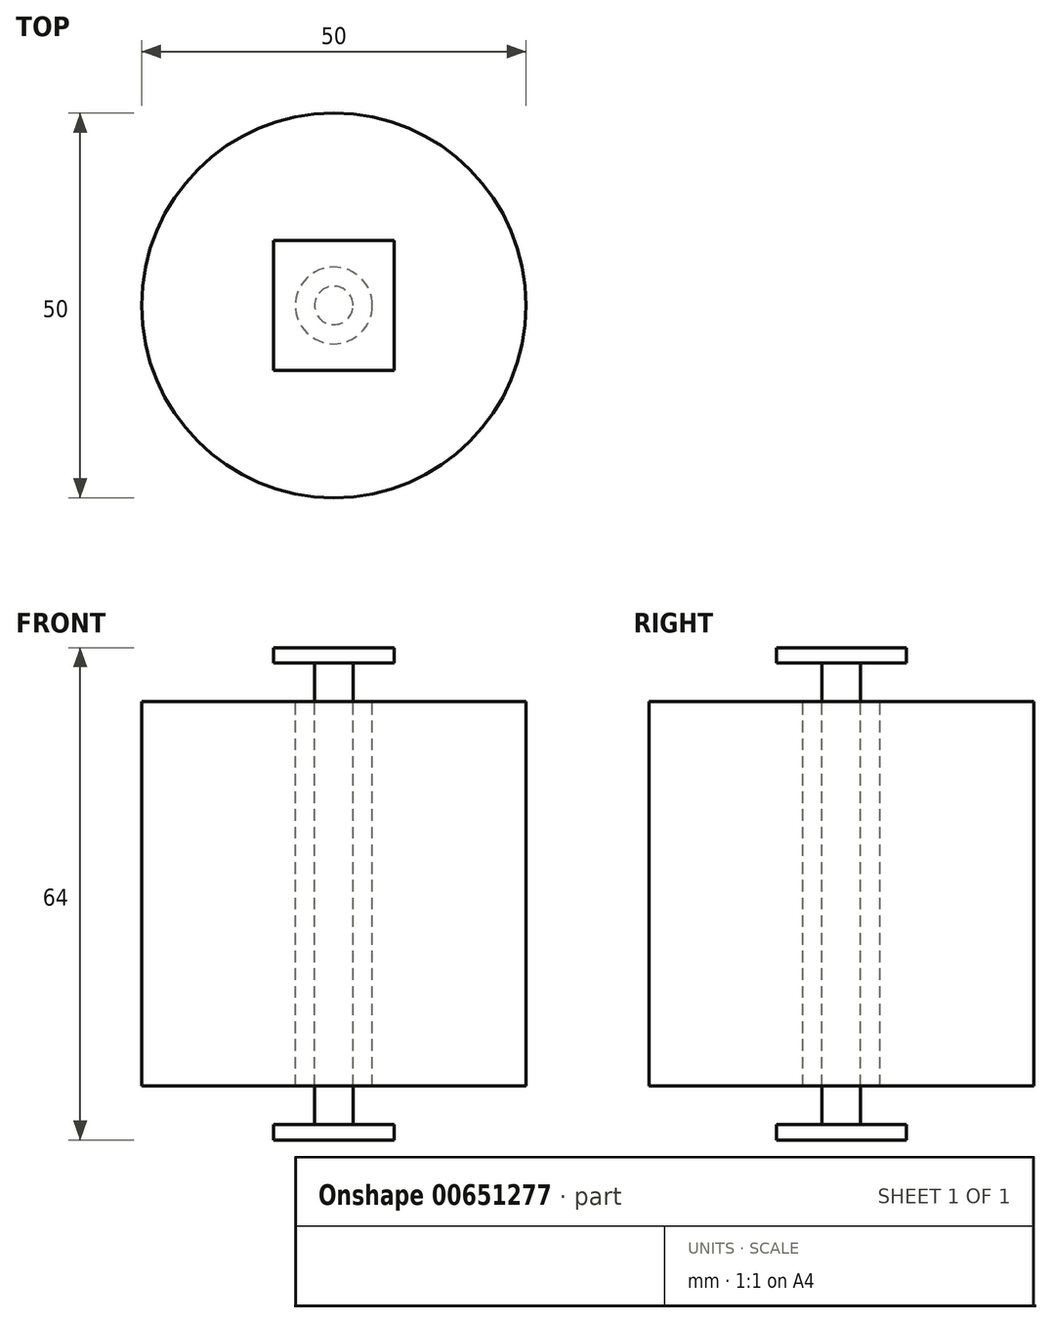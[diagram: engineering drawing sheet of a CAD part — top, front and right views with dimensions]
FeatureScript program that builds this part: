
annotation { "Feature Type Name" : "Feature", "Feature Type Description" : "" }
export const myFeature = defineFeature(function(context is Context, id is Id, definition is map)
    precondition{}
    {
        {
            var Q0;
            Q0=qCreatedBy(makeId("Top.planeOp"),FACE);
            var sketch = newSketch(context, id + "F0", { "sketchPlane" : qUnion([Q0])});
            skCircle(sketch, "E0", {"center": v(0, 0) * mm, "radius": 25 * mm});
            skSolve(sketch);
        }
        {
            var Q0;
            Q0 = qSketchRegion(id + "F0", true);
            extrude(context, id + "F1", {"entities" : qUnion([Q0]), "depth" : 50 * mm, "offsetDistance" : 25 * mm});
        }
        {
            var Q0;
            Q0=makeQuery(id+"F1.opExtrude","CAP_FACE",FACE,{"disambiguationData":[OSD([sQuery(id+"F0.wireOp",EDGE,"E0")])],"isStart":false});
            cPlane(context, id + "F2", {"entities" : qUnion([Q0]), "cplaneType" : CPlaneType.OFFSET, "offset" : 25 * mm, "oppositeDirection" : true, "width" : 150 * mm, "height" : 150 * mm});
        }
        {
            var Q0;
            Q0=qCreatedBy(id+"F2.planeOp",FACE);
            var sketch = newSketch(context, id + "F3", { "sketchPlane" : qUnion([Q0])});
            skCircle(sketch, "E1", {"center": v(0, 0) * mm, "radius": 5 * mm});
            skSolve(sketch);
        }
        {
            var Q0;
            Q0 = qSketchRegion(id + "F3", true);
            extrude(context, id + "F4", {"entities" : qUnion([Q0]), "operationType" : NewBodyOperationType.REMOVE, "endBound" : BoundingType.SYMMETRIC, "oppositeDirection" : true, "depth" : 50 * mm, "offsetDistance" : 25 * mm});
        }
        {
            var Q0;
            Q0=qCreatedBy(id+"F2.planeOp",FACE);
            var sketch = newSketch(context, id + "F5", { "sketchPlane" : qUnion([Q0])});
            skCircle(sketch, "E2", {"center": v(0, 0) * mm, "radius": 2.5 * mm});
            skSolve(sketch);
        }
        {
            var Q0;
            Q0 = qSketchRegion(id + "F5", true);
            extrude(context, id + "F6", {"entities" : qUnion([Q0]), "endBound" : BoundingType.SYMMETRIC, "depth" : 60 * mm, "offsetDistance" : 25 * mm});
        }
        {
            var Q0;
            Q0=makeQuery(id+"F6.opExtrude","CAP_FACE",FACE,{"disambiguationData":[OSD([sQuery(id+"F5.wireOp",EDGE,"E2")])],"isStart":false});
            var sketch = newSketch(context, id + "F7", { "sketchPlane" : qUnion([Q0])});
            skLineSegment(sketch, "E3.bottom", {"start": v(-7.85, 8.45) * mm, "end": v(7.85, 8.45) * mm});
            skLineSegment(sketch, "E3.top", {"start": v(-7.85, -8.45) * mm, "end": v(7.85, -8.45) * mm});
            skLineSegment(sketch, "E3.left", {"start": v(-7.85, 8.45) * mm, "end": v(-7.85, -8.45) * mm});
            skLineSegment(sketch, "E3.right", {"start": v(7.85, 8.45) * mm, "end": v(7.85, -8.45) * mm});
            skPoint(sketch, "E3.middle", {"position": v(0, 0) * mm});
            skSolve(sketch);
        }
        {
            var Q0;
            Q0=makeQuery(id+"F7.imprint","IMPRINT",FACE,{"disambiguationData":[TD([[makeQuery(id+"F7.imprint","IMPRINT",EDGE,{"derivedFrom":makeQuery(id+"F6.opExtrude","CAP_EDGE",EDGE,{"disambiguationData":[OSD([sQuery(id+"F5.wireOp",EDGE,"E2")])],"isStart":false})}),1.0]])]});
            var Q1;
            Q1=makeQuery(id+"F7.imprint","IMPRINT",FACE,{"disambiguationData":[TD([[makeQuery(id+"F7.imprint","IMPRINT",EDGE,{"derivedFrom":sQuery(id+"F7.wireOp",EDGE,"E3.bottom")}),-1.0]])]});
            extrude(context, id + "F8", {"entities" : qUnion([Q0, Q1]), "operationType" : NewBodyOperationType.ADD, "depth" : 2 * mm, "offsetDistance" : 25 * mm});
        }
        {
            var Q0;
            Q0=makeQuery(id+"F6.opExtrude","SWEPT_BODY",BODY,{"disambiguationData":[OSD([sQuery(id+"F5.wireOp",EDGE,"E2")])]});
            var Q1;
            Q1=qCreatedBy(id+"F2.planeOp",FACE);
            mirror(context, id + "F9", {"operationType" : NewBodyOperationType.ADD, "entities" : qUnion([Q0]), "mirrorPlane" : qUnion([Q1])});
        }
    });
